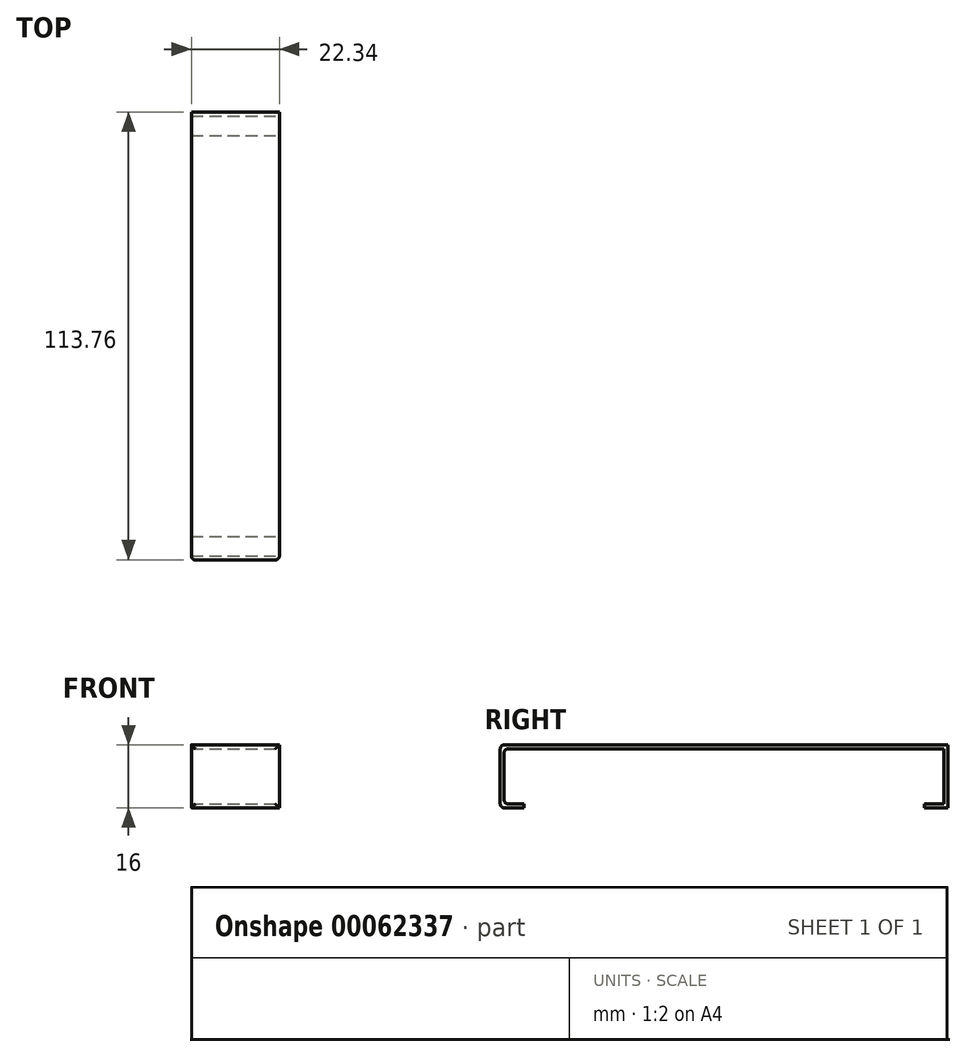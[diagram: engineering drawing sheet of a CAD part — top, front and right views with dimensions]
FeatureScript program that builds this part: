
annotation { "Feature Type Name" : "Feature", "Feature Type Description" : "" }
export const myFeature = defineFeature(function(context is Context, id is Id, definition is map)
    precondition{}
    {
        {
            var Q0;
            Q0=qCreatedBy(makeId("Top.planeOp"),FACE);
            var sketch = newSketch(context, id + "F0", { "sketchPlane" : qUnion([Q0])});
            skLineSegment(sketch, "E0.bottom", {"start": v(-31.65, 49.07) * mm, "end": v(-20.48, 49.07) * mm, "construction": true});
            skLineSegment(sketch, "E0.top", {"start": v(-31.65, -62.7) * mm, "end": v(13.03, -62.7) * mm, "construction": true});
            skLineSegment(sketch, "E0.left", {"start": v(-36.65, 44.07) * mm, "end": v(-36.65, -57.7) * mm, "construction": true});
            skLineSegment(sketch, "E0.right", {"start": v(18.03, 44.07) * mm, "end": v(18.03, -57.7) * mm, "construction": true});
            skPoint(sketch, "E1.visualSharp", {"position": v(18.03, -62.7) * mm});
            skArc(sketch, "E1.filletArc", {"start": v(13.03, -62.7) * mm, "mid": v(16.56, -61.23) * mm, "end": v(18.03, -57.7) * mm, "construction": true});
            skPoint(sketch, "E2.visualSharp", {"position": v(18.03, 49.07) * mm});
            skArc(sketch, "E2.filletArc", {"start": v(18.03, 44.07) * mm, "mid": v(16.56, 47.6) * mm, "end": v(13.03, 49.07) * mm, "construction": true});
            skPoint(sketch, "E3.visualSharp", {"position": v(-36.65, 49.07) * mm});
            skArc(sketch, "E3.filletArc", {"start": v(-31.65, 49.07) * mm, "mid": v(-35.19, 47.6) * mm, "end": v(-36.65, 44.07) * mm, "construction": true});
            skPoint(sketch, "E4.visualSharp", {"position": v(-36.65, -62.7) * mm});
            skArc(sketch, "E4.filletArc", {"start": v(-36.65, -57.7) * mm, "mid": v(-35.19, -61.23) * mm, "end": v(-31.65, -62.7) * mm, "construction": true});
            skLineSegment(sketch, "E5", {"start": v(-9.31, 49.07) * mm, "end": v(1.86, 49.07) * mm, "construction": true});
            skLineSegment(sketch, "E6", {"start": v(-20.48, 49.07) * mm, "end": v(-9.31, 49.07) * mm, "construction": true});
            skLineSegment(sketch, "E7", {"start": v(1.86, 49.07) * mm, "end": v(13.03, 49.07) * mm, "construction": true});
            skLineSegment(sketch, "E8.top", {"start": v(-20.48, -62.7) * mm, "end": v(1.86, -62.7) * mm});
            skLineSegment(sketch, "E8.left", {"start": v(-20.48, 49.07) * mm, "end": v(-20.48, -62.7) * mm});
            skLineSegment(sketch, "E8.right", {"start": v(1.86, 49.07) * mm, "end": v(1.86, -62.7) * mm});
            skLineSegment(sketch, "E9", {"start": v(-20.48, 49.07) * mm, "end": v(1.86, 49.07) * mm});
            skSolve(sketch);
        }
        {
            var Q0;
            Q0=makeQuery(id+"F0.imprint","IMPRINT",FACE,{"disambiguationData":[TD([[makeQuery(id+"F0.imprint","IMPRINT",EDGE,{"derivedFrom":sQuery(id+"F0.wireOp",EDGE,"E8.top")}),1.0]])]});
            extrude(context, id + "F1", {"entities" : qUnion([Q0]), "depth" : 1 * mm});
        }
        {
            var Q0;
            Q0=makeQuery(id+"F1.opExtrude","SWEPT_FACE",FACE,{"disambiguationData":[OSD([sQuery(id+"F0.wireOp",EDGE,"E8.top")])]});
            extrude(context, id + "F2", {"entities" : qUnion([Q0]), "depth" : 1 * mm});
        }
        {
            var Q0;
            Q0=makeQuery(id+"F1.opExtrude","SWEPT_FACE",FACE,{"disambiguationData":[OSD([sQuery(id+"F0.wireOp",EDGE,"E9")])]});
            extrude(context, id + "F3", {"entities" : qUnion([Q0]), "depth" : 1 * mm});
        }
        {
            var Q0;
            {var subQ0=sQuery(id+"F0.wireOp",EDGE,"E9");Q0=makeQuery(id+"F3.opExtrude","SWEPT_FACE",FACE,{"disambiguationData":[OSD([subQ0]),TDD([makeQuery(id+"F1.opExtrude","CAP_EDGE",EDGE,{"disambiguationData":[OSD([subQ0])],"isStart":true})])]});}
            extrude(context, id + "F4", {"entities" : qUnion([Q0]), "depth" : 14 * mm});
        }
        {
            var Q0;
            {var subQ0=sQuery(id+"F0.wireOp",EDGE,"E8.top");Q0=makeQuery(id+"F2.opExtrude","SWEPT_FACE",FACE,{"disambiguationData":[OSD([subQ0]),TDD([makeQuery(id+"F1.opExtrude","CAP_EDGE",EDGE,{"disambiguationData":[OSD([subQ0])],"isStart":true})])]});}
            extrude(context, id + "F5", {"entities" : qUnion([Q0]), "depth" : 14 * mm});
        }
        {
            var Q0;
            Q0=makeQuery(id+"F5.opExtrude","CAP_FACE",FACE,{"disambiguationData":[OSD([sQuery(id+"F0.wireOp",EDGE,"E8.top")])],"isStart":false});
            extrude(context, id + "F6", {"entities" : qUnion([Q0]), "depth" : 1 * mm});
        }
        {
            var Q0;
            Q0=makeQuery(id+"F4.opExtrude","CAP_FACE",FACE,{"disambiguationData":[OSD([sQuery(id+"F0.wireOp",EDGE,"E9")])],"isStart":false});
            extrude(context, id + "F7", {"entities" : qUnion([Q0]), "depth" : 1 * mm});
        }
        {
            var Q0;
            {var subQ0=sQuery(id+"F0.wireOp",EDGE,"E8.top");Q0=makeQuery(id+"F6.opExtrude","SWEPT_FACE",FACE,{"disambiguationData":[OSD([subQ0]),TDD([makeQuery(id+"F5.opExtrude","CAP_EDGE",EDGE,{"disambiguationData":[OSD([subQ0]),TDD([makeQuery(id+"F2.opExtrude","CAP_EDGE",EDGE,{"disambiguationData":[OSD([subQ0]),TDD([makeQuery(id+"F1.opExtrude","CAP_EDGE",EDGE,{"disambiguationData":[OSD([subQ0])],"isStart":true})])],"isStart":true})])],"isStart":false})])]});}
            extrude(context, id + "F8", {"entities" : qUnion([Q0]), "depth" : 5 * mm});
        }
        {
            var Q0;
            {var subQ0=sQuery(id+"F0.wireOp",EDGE,"E9");Q0=makeQuery(id+"F7.opExtrude","SWEPT_FACE",FACE,{"disambiguationData":[OSD([subQ0]),TDD([makeQuery(id+"F4.opExtrude","CAP_EDGE",EDGE,{"disambiguationData":[OSD([subQ0]),TDD([makeQuery(id+"F3.opExtrude","CAP_EDGE",EDGE,{"disambiguationData":[OSD([subQ0]),TDD([makeQuery(id+"F1.opExtrude","CAP_EDGE",EDGE,{"disambiguationData":[OSD([subQ0])],"isStart":true})])],"isStart":true})])],"isStart":false})])]});}
            extrude(context, id + "F9", {"entities" : qUnion([Q0]), "depth" : 5 * mm});
        }
        {
            var Q0;
            Q0=makeQuery(id+"F8.opExtrude","SWEPT_BODY",BODY,{"disambiguationData":[OSD([sQuery(id+"F0.wireOp",EDGE,"E8.top")])]});
            var Q1;
            Q1=makeQuery(id+"F6.opExtrude","SWEPT_BODY",BODY,{"disambiguationData":[OSD([sQuery(id+"F0.wireOp",EDGE,"E8.top")])]});
            var Q2;
            Q2=makeQuery(id+"F5.opExtrude","SWEPT_BODY",BODY,{"disambiguationData":[OSD([sQuery(id+"F0.wireOp",EDGE,"E8.top")])]});
            var Q3;
            Q3=makeQuery(id+"F2.opExtrude","SWEPT_BODY",BODY,{"disambiguationData":[OSD([sQuery(id+"F0.wireOp",EDGE,"E8.top")])]});
            var Q4;
            Q4=makeQuery(id+"F1.opExtrude","SWEPT_BODY",BODY,{"disambiguationData":[OSD([sQuery(id+"F0.wireOp",EDGE,"E8.top"),sQuery(id+"F0.wireOp",EDGE,"E8.left"),sQuery(id+"F0.wireOp",EDGE,"E8.right"),sQuery(id+"F0.wireOp",EDGE,"E9")])]});
            var Q5;
            Q5=makeQuery(id+"F3.opExtrude","SWEPT_BODY",BODY,{"disambiguationData":[OSD([sQuery(id+"F0.wireOp",EDGE,"E9")])]});
            var Q6;
            Q6=makeQuery(id+"F4.opExtrude","SWEPT_BODY",BODY,{"disambiguationData":[OSD([sQuery(id+"F0.wireOp",EDGE,"E9")])]});
            var Q7;
            Q7=makeQuery(id+"F9.opExtrude","SWEPT_BODY",BODY,{"disambiguationData":[OSD([sQuery(id+"F0.wireOp",EDGE,"E9")])]});
            var Q8;
            Q8=makeQuery(id+"F7.opExtrude","SWEPT_BODY",BODY,{"disambiguationData":[OSD([sQuery(id+"F0.wireOp",EDGE,"E9")])]});
            booleanBodies(context, id + "F10", {"operationType" : BooleanOperationType.UNION, "tools" : qUnion([Q0, Q1, Q2, Q3, Q4, Q5, Q6, Q7, Q8])});
        }
        {
            var Q0;
            {var subQ0=sQuery(id+"F0.wireOp",EDGE,"E8.top");Q0=makeQuery(id+"F5.opExtrude","CAP_EDGE",EDGE,{"disambiguationData":[OSD([subQ0]),TDD([makeQuery(id+"F2.opExtrude","CAP_EDGE",EDGE,{"disambiguationData":[OSD([subQ0]),TDD([makeQuery(id+"F1.opExtrude","CAP_EDGE",EDGE,{"disambiguationData":[OSD([subQ0])],"isStart":true})])],"isStart":true})])],"isStart":true});}
            var Q1;
            {var subQ0=sQuery(id+"F0.wireOp",EDGE,"E8.top");var subQ1=makeQuery(id+"F2.opExtrude","CAP_EDGE",EDGE,{"disambiguationData":[OSD([subQ0]),TDD([makeQuery(id+"F1.opExtrude","CAP_EDGE",EDGE,{"disambiguationData":[OSD([subQ0])],"isStart":true})])],"isStart":false});Q1=makeQuery(id+"F10.opBoolean","MERGE",FACE,{"derivedFrom":[makeQuery(id+"F2.opExtrude","CAP_FACE",FACE,{"disambiguationData":[OSD([subQ0])],"isStart":false}),makeQuery(id+"F5.opExtrude","SWEPT_FACE",FACE,{"disambiguationData":[OSD([subQ0]),TDD([subQ1])]}),makeQuery(id+"F6.opExtrude","SWEPT_FACE",FACE,{"disambiguationData":[OSD([subQ0]),TDD([makeQuery(id+"F5.opExtrude","CAP_EDGE",EDGE,{"disambiguationData":[OSD([subQ0]),TDD([subQ1])],"isStart":false})])]})]});}
            var Q2;
            {var subQ0=sQuery(id+"F0.wireOp",EDGE,"E8.top");Q2=makeQuery(id+"F8.opExtrude","CAP_EDGE",EDGE,{"disambiguationData":[OSD([subQ0]),TDD([makeQuery(id+"F6.opExtrude","CAP_EDGE",EDGE,{"disambiguationData":[OSD([subQ0]),TDD([makeQuery(id+"F5.opExtrude","CAP_EDGE",EDGE,{"disambiguationData":[OSD([subQ0]),TDD([makeQuery(id+"F2.opExtrude","CAP_EDGE",EDGE,{"disambiguationData":[OSD([subQ0]),TDD([makeQuery(id+"F1.opExtrude","CAP_EDGE",EDGE,{"disambiguationData":[OSD([subQ0])],"isStart":true})])],"isStart":true})])],"isStart":false})])],"isStart":true})])],"isStart":true});}
            fillet(context, id + "F11", {"entities" : qUnion([Q0, Q1, Q2]), "radius" : 1 * mm, "tangentPropagation" : true, "allowEdgeOverflow" : false});
        }
    });
